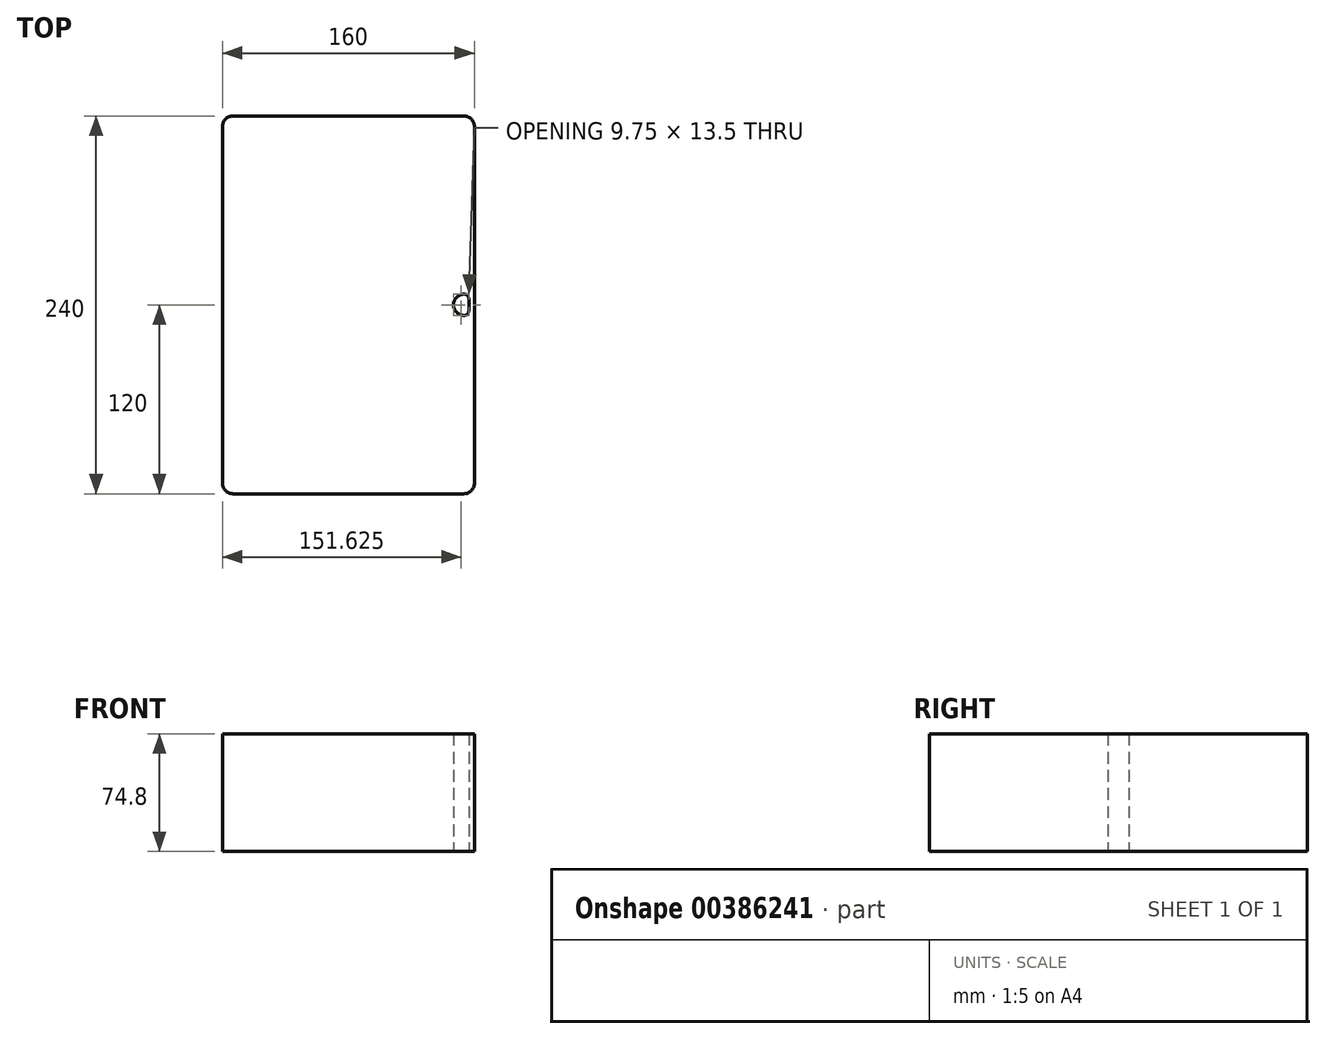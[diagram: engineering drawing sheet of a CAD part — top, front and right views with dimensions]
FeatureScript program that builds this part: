
annotation { "Feature Type Name" : "Feature", "Feature Type Description" : "" }
export const myFeature = defineFeature(function(context is Context, id is Id, definition is map)
    precondition{}
    {
        {
            var Q0;
            Q0=qCreatedBy(makeId("Top.planeOp"),FACE);
            var sketch = newSketch(context, id + "F0", { "sketchPlane" : qUnion([Q0])});
            skLineSegment(sketch, "E0.bottom", {"start": v(80, 120) * mm, "end": v(-80, 120) * mm});
            skLineSegment(sketch, "E0.top", {"start": v(80, -120) * mm, "end": v(-80, -120) * mm});
            skLineSegment(sketch, "E0.left", {"start": v(80, 120) * mm, "end": v(80, -120) * mm});
            skLineSegment(sketch, "E0.right", {"start": v(-80, 120) * mm, "end": v(-80, -120) * mm});
            skPoint(sketch, "E0.middle", {"position": v(0, 0) * mm});
            skLineSegment(sketch, "E1.bottom", {"start": v(76.5, 116.5) * mm, "end": v(-76.5, 116.5) * mm});
            skLineSegment(sketch, "E1.top", {"start": v(76.5, -116.5) * mm, "end": v(-76.5, -116.5) * mm});
            skLineSegment(sketch, "E1.left", {"start": v(76.5, 116.5) * mm, "end": v(76.5, -116.5) * mm});
            skLineSegment(sketch, "E1.right", {"start": v(-76.5, 116.5) * mm, "end": v(-76.5, -116.5) * mm});
            skPoint(sketch, "E2.endSnap0", {"position": v(-76.5, 0) * mm});
            skArc(sketch, "E3", {"start": v(-64.85, 106.7) * mm, "mid": v(-60.08, 108.68) * mm, "end": v(-58.1, 113.45) * mm});
            skLineSegment(sketch, "E4", {"start": v(-58.1, 113.45) * mm, "end": v(-58.1, 116.5) * mm});
            skLineSegment(sketch, "E5", {"start": v(-64.85, 106.7) * mm, "end": v(-76.5, 106.7) * mm});
            skArc(sketch, "E6", {"start": v(64.85, -106.7) * mm, "mid": v(60.08, -108.68) * mm, "end": v(58.1, -113.45) * mm});
            skLineSegment(sketch, "E7", {"start": v(58.1, -113.45) * mm, "end": v(58.1, -116.5) * mm});
            skLineSegment(sketch, "E8", {"start": v(64.85, -106.7) * mm, "end": v(76.5, -106.7) * mm});
            skArc(sketch, "E9", {"start": v(58.1, 113.45) * mm, "mid": v(60.08, 108.68) * mm, "end": v(64.85, 106.7) * mm});
            skLineSegment(sketch, "E10", {"start": v(64.85, 106.7) * mm, "end": v(76.5, 106.7) * mm});
            skLineSegment(sketch, "E11", {"start": v(58.1, 113.45) * mm, "end": v(58.1, 116.5) * mm});
            skLineSegment(sketch, "E12", {"start": v(-76.5, -106.7) * mm, "end": v(-64.72, -106.7) * mm});
            skLineSegment(sketch, "E13", {"start": v(-58.1, -112.13) * mm, "end": v(-58.1, -116.5) * mm});
            skArc(sketch, "E14", {"start": v(-58.1, -112.13) * mm, "mid": v(-60.44, -108.23) * mm, "end": v(-64.72, -106.7) * mm});
            skLineSegment(sketch, "E15", {"start": v(76.5, 0) * mm, "end": v(73.5, 0) * mm, "construction": true});
            skPoint(sketch, "E15.endSnap0", {"position": v(76.5, 0) * mm});
            skArc(sketch, "E16", {"start": v(73.5, -6.75) * mm, "mid": v(66.75, 0) * mm, "end": v(73.5, 6.75) * mm});
            skLineSegment(sketch, "E17", {"start": v(73.5, 6.75) * mm, "end": v(76.5, 6.75) * mm});
            skLineSegment(sketch, "E18", {"start": v(73.5, -6.75) * mm, "end": v(76.5, -6.75) * mm});
            skLineSegment(sketch, "E19", {"start": v(-76.5, 0) * mm, "end": v(-73.5, 0) * mm, "construction": true});
            skArc(sketch, "E20", {"start": v(-73.5, -6.75) * mm, "mid": v(-66.75, 0) * mm, "end": v(-73.5, 6.75) * mm});
            skLineSegment(sketch, "E21", {"start": v(-73.5, 6.75) * mm, "end": v(-76.5, 6.75) * mm});
            skLineSegment(sketch, "E22", {"start": v(-73.5, -6.75) * mm, "end": v(-76.5, -6.75) * mm});
            skSolve(sketch);
        }
        {
            var Q0;
            Q0=makeQuery(id+"F0.imprint","IMPRINT",FACE,{"disambiguationData":[TD([[makeQuery(id+"F0.imprint","IMPRINT",EDGE,{"derivedFrom":sQuery(id+"F0.wireOp",EDGE,"E3")}),-1.0]])]});
            extrude(context, id + "F1", {"entities" : qUnion([Q0]), "depth" : 3 * mm, "offsetDistance" : 25 * mm});
        }
        {
            var Q0;
            Q0 = qSketchRegion(id + "F0", true);
            var Q1;
            Q1=makeQuery(id+"F0.imprint","IMPRINT",FACE,{"disambiguationData":[TD([[makeQuery(id+"F0.imprint","IMPRINT",EDGE,{"derivedFrom":sQuery(id+"F0.wireOp",EDGE,"E3")}),1.0]])]});
            var Q2;
            Q2=makeQuery(id+"F0.imprint","IMPRINT",FACE,{"disambiguationData":[TD([[makeQuery(id+"F0.imprint","IMPRINT",EDGE,{"derivedFrom":sQuery(id+"F0.wireOp",EDGE,"E9")}),1.0]])]});
            var Q3;
            Q3=makeQuery(id+"F0.imprint","IMPRINT",FACE,{"disambiguationData":[TD([[makeQuery(id+"F0.imprint","IMPRINT",EDGE,{"derivedFrom":sQuery(id+"F0.wireOp",EDGE,"E20")}),1.0]])]});
            var Q4;
            Q4=makeQuery(id+"F0.imprint","IMPRINT",FACE,{"disambiguationData":[TD([[makeQuery(id+"F0.imprint","IMPRINT",EDGE,{"derivedFrom":sQuery(id+"F0.wireOp",EDGE,"E16")}),-1.0]])]});
            var Q5;
            {var subQ4=sQuery(id+"F0.wireOp",EDGE,"E12");Q5=makeQuery(id+"F0.imprint","IMPRINT",FACE,{"disambiguationData":[TD([[makeQuery(id+"F0.imprint","IMPRINT",EDGE,{"derivedFrom":subQ4}),-1.0]])]});}
            var Q6;
            Q6=makeQuery(id+"F0.imprint","IMPRINT",FACE,{"disambiguationData":[TD([[makeQuery(id+"F0.imprint","IMPRINT",EDGE,{"derivedFrom":sQuery(id+"F0.wireOp",EDGE,"E6")}),1.0]])]});
            extrude(context, id + "F2", {"entities" : qUnion([Q0, Q1, Q2, Q3, Q4, Q5, Q6]), "operationType" : NewBodyOperationType.ADD, "depth" : 74.8 * mm, "offsetDistance" : 25 * mm});
        }
        {
            var Q0;
            Q0=makeQuery(id+"F2.opExtrude","SWEPT_EDGE",EDGE,{"disambiguationData":[OSD([sQuery(id+"F0.wireOp",EDGE,"E0.bottom"),sQuery(id+"F0.wireOp",EDGE,"E0.left")])]});
            var Q1;
            Q1=makeQuery(id+"F2.opExtrude","SWEPT_EDGE",EDGE,{"disambiguationData":[OSD([sQuery(id+"F0.wireOp",EDGE,"E0.bottom"),sQuery(id+"F0.wireOp",EDGE,"E0.right")])]});
            var Q2;
            Q2=makeQuery(id+"F2.opExtrude","SWEPT_EDGE",EDGE,{"disambiguationData":[OSD([sQuery(id+"F0.wireOp",EDGE,"E0.top"),sQuery(id+"F0.wireOp",EDGE,"E0.right")])]});
            var Q3;
            Q3=makeQuery(id+"F2.opExtrude","SWEPT_EDGE",EDGE,{"disambiguationData":[OSD([sQuery(id+"F0.wireOp",EDGE,"E0.top"),sQuery(id+"F0.wireOp",EDGE,"E0.left")])]});
            fillet(context, id + "F3", {"entities" : qUnion([Q0, Q1, Q2, Q3]), "radius" : 6.75 * mm, "tangentPropagation" : true, "allowEdgeOverflow" : false});
        }
        {
            var Q0;
            Q0=makeQuery(id+"F2.opExtrude","SWEPT_EDGE",EDGE,{"disambiguationData":[OSD([sQuery(id+"F0.wireOp",EDGE,"E1.right"),sQuery(id+"F0.wireOp",EDGE,"E5")])]});
            var Q1;
            Q1=makeQuery(id+"F2.opExtrude","SWEPT_EDGE",EDGE,{"disambiguationData":[OSD([sQuery(id+"F0.wireOp",EDGE,"E1.bottom"),sQuery(id+"F0.wireOp",EDGE,"E4")])]});
            var Q2;
            Q2=makeQuery(id+"F2.opExtrude","SWEPT_EDGE",EDGE,{"disambiguationData":[OSD([sQuery(id+"F0.wireOp",EDGE,"E1.right"),sQuery(id+"F0.wireOp",EDGE,"E22")])]});
            var Q3;
            Q3=makeQuery(id+"F2.opExtrude","SWEPT_EDGE",EDGE,{"disambiguationData":[OSD([sQuery(id+"F0.wireOp",EDGE,"E1.bottom"),sQuery(id+"F0.wireOp",EDGE,"E11")])]});
            var Q4;
            Q4=makeQuery(id+"F2.opExtrude","SWEPT_EDGE",EDGE,{"disambiguationData":[OSD([sQuery(id+"F0.wireOp",EDGE,"E1.left"),sQuery(id+"F0.wireOp",EDGE,"E10")])]});
            var Q5;
            Q5=makeQuery(id+"F2.opExtrude","SWEPT_EDGE",EDGE,{"disambiguationData":[OSD([sQuery(id+"F0.wireOp",EDGE,"E1.left"),sQuery(id+"F0.wireOp",EDGE,"E18")])]});
            var Q6;
            Q6=makeQuery(id+"F2.opExtrude","SWEPT_EDGE",EDGE,{"disambiguationData":[OSD([sQuery(id+"F0.wireOp",EDGE,"E1.right"),sQuery(id+"F0.wireOp",EDGE,"E21")])]});
            var Q7;
            Q7=makeQuery(id+"F2.opExtrude","SWEPT_EDGE",EDGE,{"disambiguationData":[OSD([sQuery(id+"F0.wireOp",EDGE,"E1.right"),sQuery(id+"F0.wireOp",EDGE,"E12")])]});
            var Q8;
            Q8=makeQuery(id+"F2.opExtrude","SWEPT_EDGE",EDGE,{"disambiguationData":[OSD([sQuery(id+"F0.wireOp",EDGE,"E1.top"),sQuery(id+"F0.wireOp",EDGE,"E13")])]});
            var Q9;
            Q9=makeQuery(id+"F2.opExtrude","SWEPT_EDGE",EDGE,{"disambiguationData":[OSD([sQuery(id+"F0.wireOp",EDGE,"E1.left"),sQuery(id+"F0.wireOp",EDGE,"E17")])]});
            var Q10;
            Q10=makeQuery(id+"F2.opExtrude","SWEPT_EDGE",EDGE,{"disambiguationData":[OSD([sQuery(id+"F0.wireOp",EDGE,"E1.left"),sQuery(id+"F0.wireOp",EDGE,"E8")])]});
            var Q11;
            Q11=makeQuery(id+"F2.opExtrude","SWEPT_EDGE",EDGE,{"disambiguationData":[OSD([sQuery(id+"F0.wireOp",EDGE,"E1.top"),sQuery(id+"F0.wireOp",EDGE,"E7")])]});
            fillet(context, id + "F4", {"entities" : qUnion([Q0, Q1, Q2, Q3, Q4, Q5, Q6, Q7, Q8, Q9, Q10, Q11]), "radius" : 3 * mm, "tangentPropagation" : true, "allowEdgeOverflow" : false});
        }
    });
